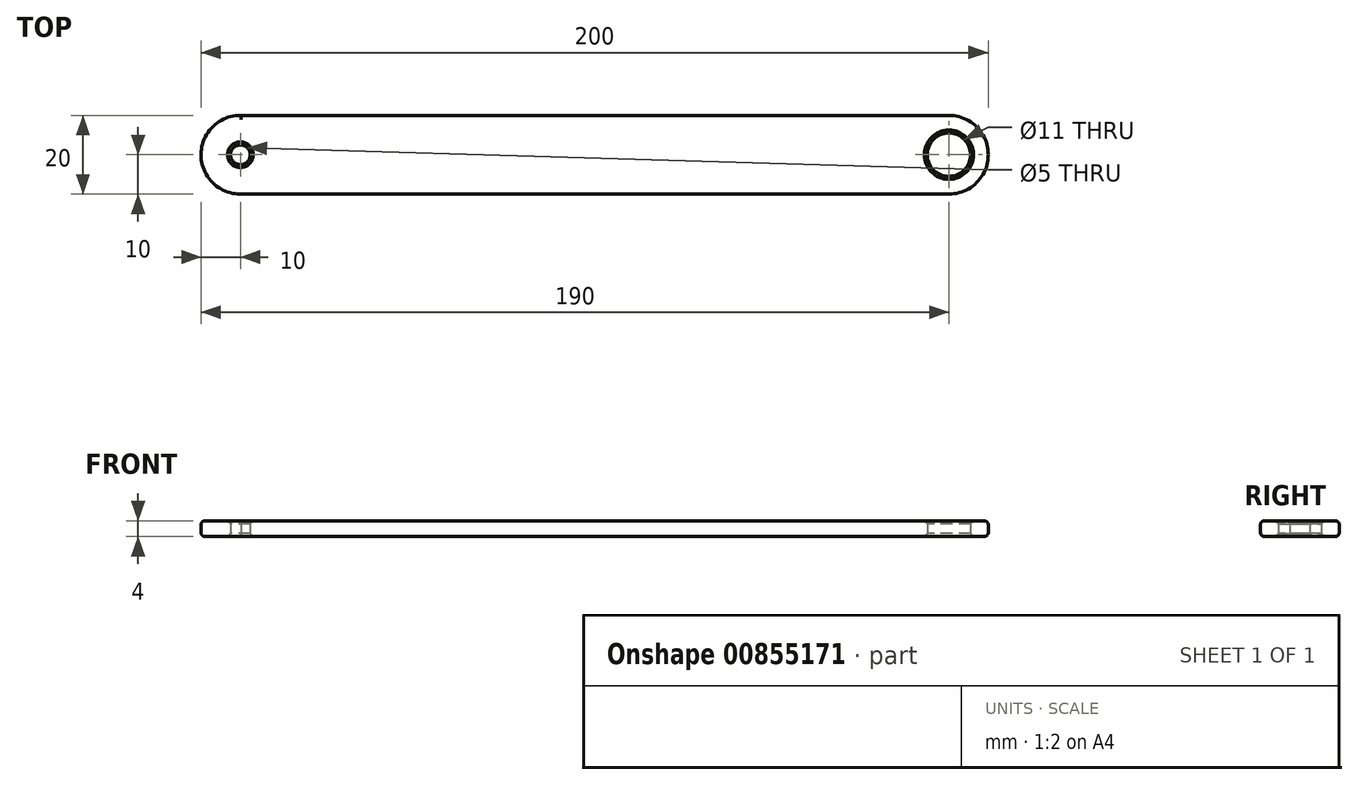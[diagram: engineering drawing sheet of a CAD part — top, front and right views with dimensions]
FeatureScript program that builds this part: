
annotation { "Feature Type Name" : "Feature", "Feature Type Description" : "" }
export const myFeature = defineFeature(function(context is Context, id is Id, definition is map)
    precondition{}
    {
        {
            var Q0;
            Q0=qCreatedBy(makeId("Top.planeOp"),FACE);
            var sketch = newSketch(context, id + "F0", { "sketchPlane" : qUnion([Q0])});
            skPoint(sketch, "E0", {"position": v(-180, 0) * mm});
            skCircle(sketch, "E1", {"center": v(-180, 0) * mm, "radius": 2.5 * mm});
            skCircle(sketch, "E2", {"center": v(-180, 0) * mm, "radius": 10 * mm});
            skCircle(sketch, "E3", {"center": v(0, 0) * mm, "radius": 5.5 * mm});
            skCircle(sketch, "E4", {"center": v(0, 0) * mm, "radius": 10 * mm});
            skLineSegment(sketch, "E5", {"start": v(-180.03, -10) * mm, "end": v(0, -10) * mm});
            skLineSegment(sketch, "E6", {"start": v(0, 10) * mm, "end": v(-179.82, 10) * mm});
            skSolve(sketch);
        }
        {
            var Q0;
            {var subQ0=sQuery(id+"F0.wireOp",EDGE,"E5");Q0=makeQuery(id+"F0.imprint","IMPRINT",FACE,{"disambiguationData":[TD([[makeQuery(id+"F0.imprint","IMPRINT",EDGE,{"derivedFrom":subQ0}),1.0]])]});}
            var Q1;
            Q1=makeQuery(id+"F0.imprint","IMPRINT",FACE,{"disambiguationData":[TD([[makeQuery(id+"F0.imprint","IMPRINT",EDGE,{"derivedFrom":sQuery(id+"F0.wireOp",EDGE,"E1")}),-1.0]])]});
            var Q2;
            Q2=makeQuery(id+"F0.imprint","IMPRINT",FACE,{"disambiguationData":[TD([[makeQuery(id+"F0.imprint","IMPRINT",EDGE,{"derivedFrom":sQuery(id+"F0.wireOp",EDGE,"E3")}),-1.0]])]});
            extrude(context, id + "F1", {"entities" : qUnion([Q0, Q1, Q2]), "depth" : 4 * mm, "offsetDistance" : 25 * mm, "symmetric" : true});
        }
        {
            var Q0;
            Q0=makeQuery(id+"F1.opExtrude","CAP_EDGE",EDGE,{"disambiguationData":[OSD([sQuery(id+"F0.wireOp",EDGE,"E2")])],"isStart":false});
            var Q1;
            Q1=makeQuery(id+"F1.opExtrude","CAP_EDGE",EDGE,{"disambiguationData":[OSD([sQuery(id+"F0.wireOp",EDGE,"E5")])],"isStart":false});
            var Q2;
            Q2=makeQuery(id+"F1.opExtrude","CAP_EDGE",EDGE,{"disambiguationData":[OSD([sQuery(id+"F0.wireOp",EDGE,"E6")])],"isStart":true});
            var Q3;
            Q3=makeQuery(id+"F1.opExtrude","CAP_EDGE",EDGE,{"disambiguationData":[OSD([sQuery(id+"F0.wireOp",EDGE,"E2")])],"isStart":true});
            fillet(context, id + "F2", {"entities" : qUnion([Q0, Q1, Q2, Q3]), "radius" : 1 * mm, "tangentPropagation" : true, "allowEdgeOverflow" : false});
        }
        {
            var Q0;
            Q0=makeQuery(id+"F1.opExtrude","CAP_EDGE",EDGE,{"disambiguationData":[OSD([sQuery(id+"F0.wireOp",EDGE,"E3")])],"isStart":false});
            var Q1;
            Q1=makeQuery(id+"F1.opExtrude","CAP_EDGE",EDGE,{"disambiguationData":[OSD([sQuery(id+"F0.wireOp",EDGE,"E3")])],"isStart":true});
            var Q2;
            Q2=makeQuery(id+"F1.opExtrude","CAP_EDGE",EDGE,{"disambiguationData":[OSD([sQuery(id+"F0.wireOp",EDGE,"E1")])],"isStart":true});
            var Q3;
            Q3=makeQuery(id+"F1.opExtrude","CAP_EDGE",EDGE,{"disambiguationData":[OSD([sQuery(id+"F0.wireOp",EDGE,"E1")])],"isStart":false});
            chamfer(context, id + "F3", {"entities" : qUnion([Q0, Q1, Q2, Q3]), "width" : 0.75 * mm, "tangentPropagation" : true});
        }
    });
